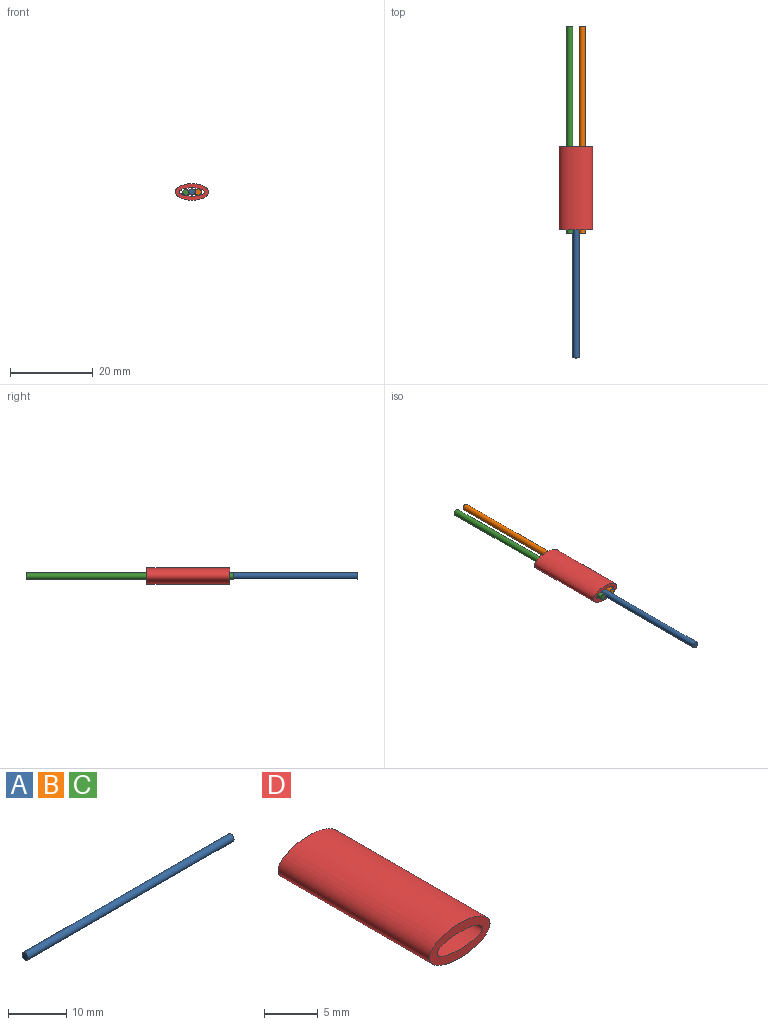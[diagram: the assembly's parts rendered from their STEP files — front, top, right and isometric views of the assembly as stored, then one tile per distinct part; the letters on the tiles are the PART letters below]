
ASSEMBLY  parts=4 mates=3
PART A: 3 faces, bbox 50x1.5x1.5 mm
  f0: plane 1.5x1.5mm, normal (-1,0,0), area 1.8mm2, adj f2
  f1: plane 1.5x1.5mm, normal (1,0,0), area 1.8mm2, adj f2
  f2: cylinder r=0.75mm len=50mm, axis (1,0,0), area 235.6mm2, adj f0,f1
PART B: same geometry as A
PART C: same geometry as A
PART D: 4 faces, bbox 8x20x4 mm
  f0: extruded ~20x6mm, area 267.4mm2, adj f2,f3
  f1: extruded ~20x8mm, area 387.6mm2, adj f2,f3
  f2: plane 8x4mm, normal (0,-1,0), area 15.7mm2, adj f0,f1
  f3: plane 8x4mm, normal (0,1,0), area 15.7mm2, adj f0,f1
PLACE A rot(axis=(0.58,0.58,0.58),120deg) t=(-13.86,-57.57,-10.79)mm
PLACE B rot(axis=(0,0,1),90deg) t=(-12.36,-27.57,-10.79)mm
PLACE C rot(axis=(0,0,1),90deg) t=(-15.35,-27.57,-10.88)mm
PLACE D t=(-13.86,-6.7,0.49)mm
MATE planar B.f2 <-> A.f2  axis (0,-1,0) through (-12.36,-27.57,-10.79)mm
MATE cylindrical A.f2 <-> D.f3  axis (0,1,0) through (-13.86,-32.57,-10.79)mm
MATE planar C.f2 <-> B.f2  axis (0,-1,0) through (-15.35,-27.57,-10.88)mm
